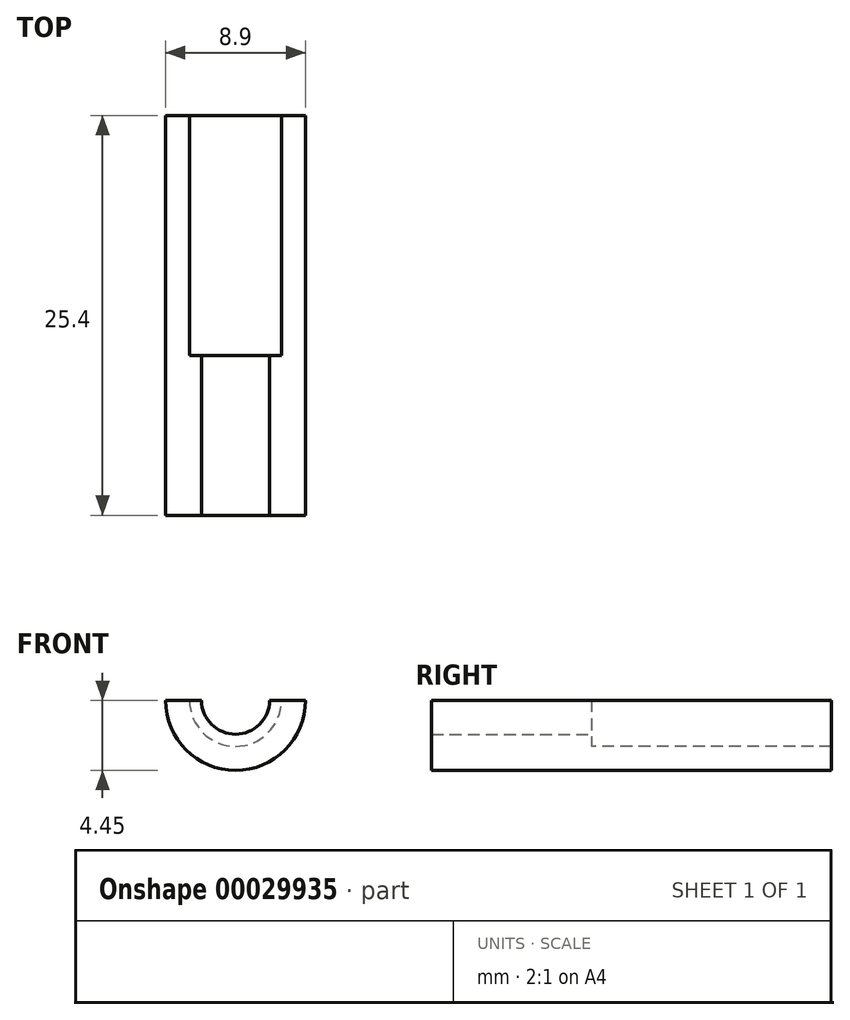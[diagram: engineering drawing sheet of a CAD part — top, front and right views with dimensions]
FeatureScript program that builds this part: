
annotation { "Feature Type Name" : "Feature", "Feature Type Description" : "" }
export const myFeature = defineFeature(function(context is Context, id is Id, definition is map)
    precondition{}
    {
        {
            var Q0;
            Q0=qCreatedBy(makeId("Front.planeOp"),FACE);
            var sketch = newSketch(context, id + "F0", { "sketchPlane" : qUnion([Q0])});
            skCircle(sketch, "E0", {"center": v(0, 0) * mm, "radius": 4.45 * mm});
            skCircle(sketch, "E1", {"center": v(0, 0) * mm, "radius": 2.16 * mm});
            skSolve(sketch);
        }
        {
            var Q0;
            Q0 = qSketchRegion(id + "F0", true);
            extrude(context, id + "F1", {"entities" : qUnion([Q0]), "depth" : 10.16 * mm});
        }
        {
            var Q0;
            Q0=qCreatedBy(makeId("Front.planeOp"),FACE);
            var sketch = newSketch(context, id + "F2", { "sketchPlane" : qUnion([Q0])});
            skCircle(sketch, "E2", {"center": v(0, 0) * mm, "radius": 2.92 * mm});
            skCircle(sketch, "E3", {"center": v(0, 0) * mm, "radius": 4.45 * mm});
            skSolve(sketch);
        }
        {
            var Q0;
            Q0 = qSketchRegion(id + "F2", true);
            extrude(context, id + "F3", {"entities" : qUnion([Q0]), "operationType" : NewBodyOperationType.ADD, "oppositeDirection" : true, "depth" : 15.24 * mm});
        }
        {
            var Q0;
            Q0=qCreatedBy(makeId("Front.planeOp"),FACE);
            var sketch = newSketch(context, id + "F4", { "sketchPlane" : qUnion([Q0])});
            skLineSegment(sketch, "E4.bottom", {"start": v(10.46, 8.3) * mm, "end": v(-9.73, 8.3) * mm});
            skLineSegment(sketch, "E4.top", {"start": v(10.46, 0) * mm, "end": v(-9.73, 0) * mm});
            skLineSegment(sketch, "E4.left", {"start": v(10.46, 8.3) * mm, "end": v(10.46, 0) * mm});
            skLineSegment(sketch, "E4.right", {"start": v(-9.73, 8.3) * mm, "end": v(-9.73, 0) * mm});
            skSolve(sketch);
        }
        {
            var Q0;
            Q0=makeQuery(id+"F4.imprint","IMPRINT",FACE,{"disambiguationData":[TD([[makeQuery(id+"F4.imprint","IMPRINT",EDGE,{"derivedFrom":sQuery(id+"F4.wireOp",EDGE,"E4.bottom")}),1.0]])]});
            extrude(context, id + "F5", {"entities" : qUnion([Q0]), "operationType" : NewBodyOperationType.REMOVE, "endBound" : BoundingType.THROUGH_ALL, "oppositeDirection" : true, "depth" : 25.4 * mm, "hasSecondDirection" : true, "secondDirectionBound" : SecondDirectionBoundingType.THROUGH_ALL, "secondDirectionOppositeDirection" : false, "secondDirectionDepth" : 25.4 * mm});
        }
    });
